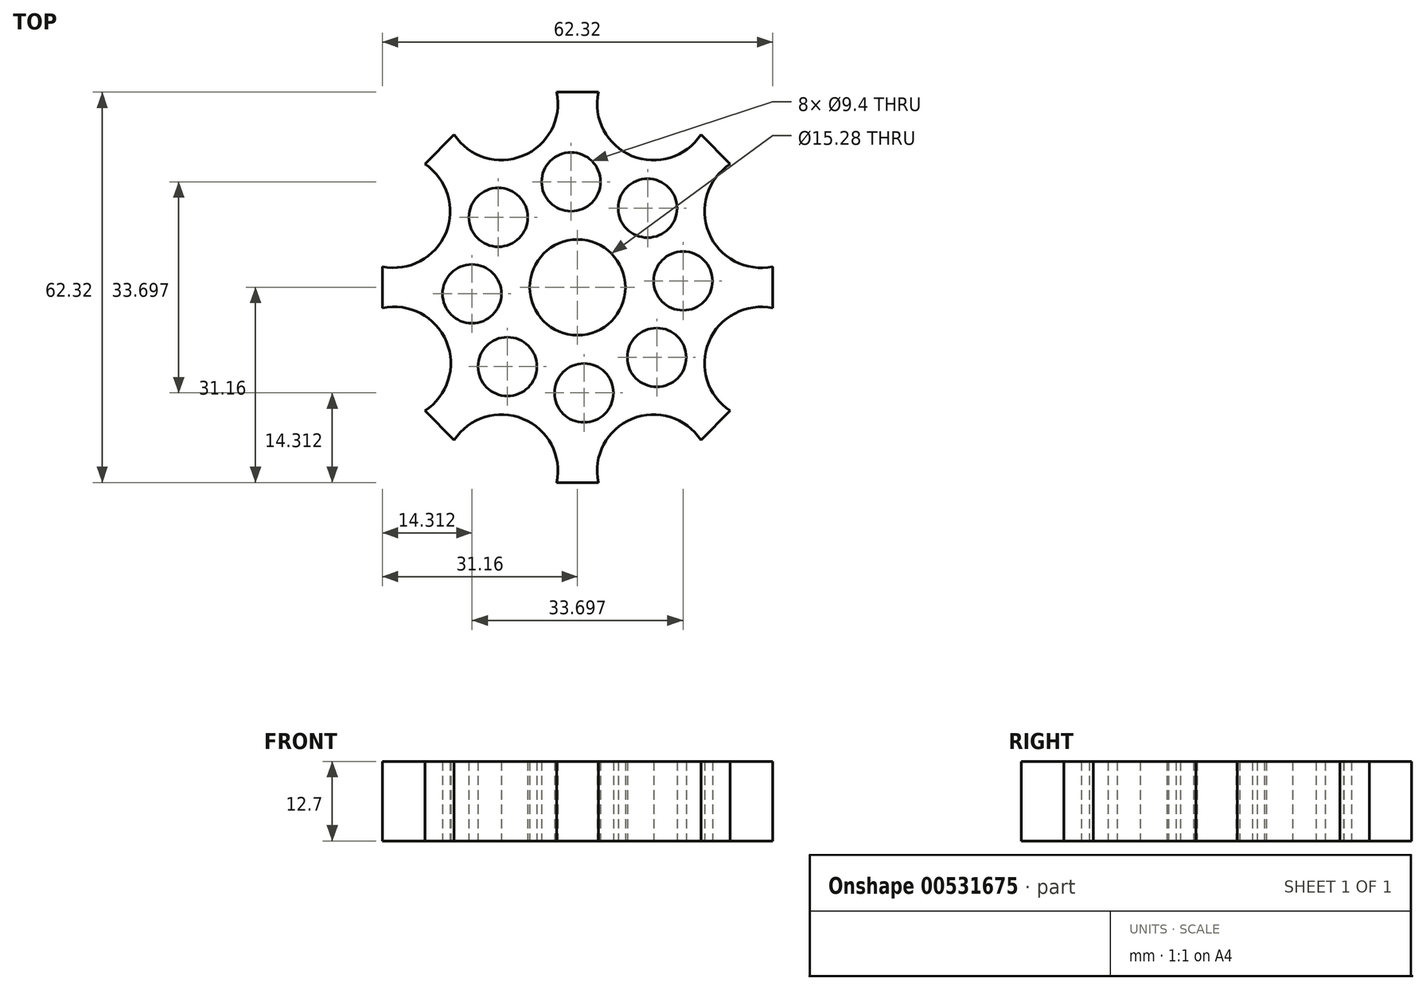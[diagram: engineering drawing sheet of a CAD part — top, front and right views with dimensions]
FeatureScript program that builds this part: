
annotation { "Feature Type Name" : "Feature", "Feature Type Description" : "" }
export const myFeature = defineFeature(function(context is Context, id is Id, definition is map)
    precondition{}
    {
        {
            var Q0;
            Q0=qCreatedBy(makeId("Top.planeOp"),FACE);
            var sketch = newSketch(context, id + "F0", { "sketchPlane" : qUnion([Q0])});
            skArc(sketch, "E0", {"start": v(-21.43, -7.63) * mm, "mid": v(-21.01, -8.7) * mm, "end": v(-20.55, -9.76) * mm});
            skLineSegment(sketch, "E1.bottom", {"start": v(0, 31.16) * mm, "end": v(-3.32, 31.16) * mm});
            skLineSegment(sketch, "E1.top", {"start": v(0, 31.16) * mm, "end": v(-3.32, 31.16) * mm});
            skLineSegment(sketch, "E1.left", {"start": v(0, 31.16) * mm, "end": v(0, 31.16) * mm});
            skLineSegment(sketch, "E1.right", {"start": v(-3.32, 31.16) * mm, "end": v(-3.32, 31.16) * mm});
            skLineSegment(sketch, "E2.MirrorCS", {"start": v(0, 31.16) * mm, "end": v(3.32, 31.16) * mm});
            skLineSegment(sketch, "E3", {"start": v(-3.32, 31.16) * mm, "end": v(3.32, 31.16) * mm});
            skLineSegment(sketch, "E4.1.0", {"start": v(-24.38, 19.69) * mm, "end": v(-19.69, 24.38) * mm});
            skLineSegment(sketch, "E4.2.0", {"start": v(-31.16, -3.32) * mm, "end": v(-31.16, 3.32) * mm});
            skLineSegment(sketch, "E4.3.0", {"start": v(-19.69, -24.38) * mm, "end": v(-24.38, -19.69) * mm});
            skLineSegment(sketch, "E4.4.0", {"start": v(3.32, -31.16) * mm, "end": v(-3.32, -31.16) * mm});
            skLineSegment(sketch, "E4.5.0", {"start": v(24.38, -19.69) * mm, "end": v(19.69, -24.38) * mm});
            skLineSegment(sketch, "E4.6.0", {"start": v(31.16, 3.32) * mm, "end": v(31.16, -3.32) * mm});
            skLineSegment(sketch, "E4.7.0", {"start": v(19.69, 24.38) * mm, "end": v(24.38, 19.69) * mm});
            skArc(sketch, "E5", {"start": v(-19.69, 24.38) * mm, "mid": v(-8.7, 21.01) * mm, "end": v(-3.32, 31.16) * mm});
            skPoint(sketch, "E5.third.point", {"position": v(-8.86, 20.95) * mm});
            skArc(sketch, "E6", {"start": v(-31.16, 3.32) * mm, "mid": v(-21.01, 8.7) * mm, "end": v(-24.38, 19.69) * mm});
            skPoint(sketch, "E6.third.point", {"position": v(-21.03, 8.67) * mm});
            skArc(sketch, "E7", {"start": v(-24.38, -19.69) * mm, "mid": v(-20.92, -8.66) * mm, "end": v(-31.16, -3.32) * mm});
            skPoint(sketch, "E7.third.point", {"position": v(-20.55, -9.76) * mm});
            skArc(sketch, "E8", {"start": v(-3.32, -31.16) * mm, "mid": v(-8.7, -20.99) * mm, "end": v(-19.69, -24.38) * mm});
            skPoint(sketch, "E8.third.point", {"position": v(-9.24, -20.78) * mm});
            skArc(sketch, "E9", {"start": v(19.69, -24.38) * mm, "mid": v(8.7, -20.99) * mm, "end": v(3.32, -31.16) * mm});
            skPoint(sketch, "E9.third.point", {"position": v(9.24, -20.78) * mm});
            skArc(sketch, "E10", {"start": v(31.16, -3.32) * mm, "mid": v(20.97, -8.69) * mm, "end": v(24.38, -19.69) * mm});
            skPoint(sketch, "E10.third.point", {"position": v(21.3, -8) * mm});
            skArc(sketch, "E11", {"start": v(24.38, 19.69) * mm, "mid": v(20.97, 8.69) * mm, "end": v(31.16, 3.32) * mm});
            skPoint(sketch, "E11.third.point", {"position": v(21.3, 8) * mm});
            skArc(sketch, "E12", {"start": v(3.32, 31.16) * mm, "mid": v(8.7, 20.99) * mm, "end": v(19.69, 24.38) * mm});
            skPoint(sketch, "E12.third.point", {"position": v(9.24, 20.78) * mm});
            skArc(sketch, "E13.trimOffspring", {"start": v(-21, 8.74) * mm, "mid": v(-21.01, 8.7) * mm, "end": v(-21.03, 8.67) * mm});
            skArc(sketch, "E14.trimOffspring", {"start": v(-8.55, 21.08) * mm, "mid": v(-8.7, 21.01) * mm, "end": v(-8.86, 20.95) * mm});
            skArc(sketch, "E15.trimOffspring", {"start": v(9.24, 20.78) * mm, "mid": v(8.7, 21.01) * mm, "end": v(8.16, 21.23) * mm});
            skArc(sketch, "E16.trimOffspring", {"start": v(21.3, 8) * mm, "mid": v(21.01, 8.7) * mm, "end": v(20.72, 9.4) * mm});
            skArc(sketch, "E17.trimOffspring", {"start": v(20.7, -9.4) * mm, "mid": v(21.01, -8.7) * mm, "end": v(21.3, -8) * mm});
            skArc(sketch, "E18.trimOffspring", {"start": v(8.16, -21.23) * mm, "mid": v(8.7, -21.01) * mm, "end": v(9.24, -20.78) * mm});
            skArc(sketch, "E19.trimOffspring", {"start": v(-9.24, -20.78) * mm, "mid": v(-8.7, -21.01) * mm, "end": v(-8.16, -21.23) * mm});
            skCircle(sketch, "E20", {"center": v(0, 0) * mm, "radius": 7.64 * mm});
            skCircle(sketch, "E21", {"center": v(11.18, 12.64) * mm, "radius": 4.7 * mm});
            skCircle(sketch, "E22.1.0", {"center": v(-1.03, 16.85) * mm, "radius": 4.7 * mm});
            skCircle(sketch, "E22.2.0", {"center": v(-12.64, 11.18) * mm, "radius": 4.7 * mm});
            skCircle(sketch, "E22.3.0", {"center": v(-16.85, -1.03) * mm, "radius": 4.7 * mm});
            skCircle(sketch, "E22.4.0", {"center": v(-11.18, -12.64) * mm, "radius": 4.7 * mm});
            skCircle(sketch, "E22.5.0", {"center": v(1.03, -16.85) * mm, "radius": 4.7 * mm});
            skCircle(sketch, "E22.6.0", {"center": v(12.64, -11.18) * mm, "radius": 4.7 * mm});
            skCircle(sketch, "E22.7.0", {"center": v(16.85, 1.03) * mm, "radius": 4.7 * mm});
            skSolve(sketch);
        }
        {
            var Q0;
            {var subQ17=sQuery(id+"F0.wireOp",EDGE,"E4.1.0");Q0=makeQuery(id+"F0.imprint","IMPRINT",FACE,{"disambiguationData":[TD([[makeQuery(id+"F0.imprint","IMPRINT",EDGE,{"derivedFrom":subQ17}),-1.0]])]});}
            extrude(context, id + "F1", {"entities" : qUnion([Q0]), "depth" : 12.7 * mm, "offsetDistance" : 25.4 * mm});
        }
    });
